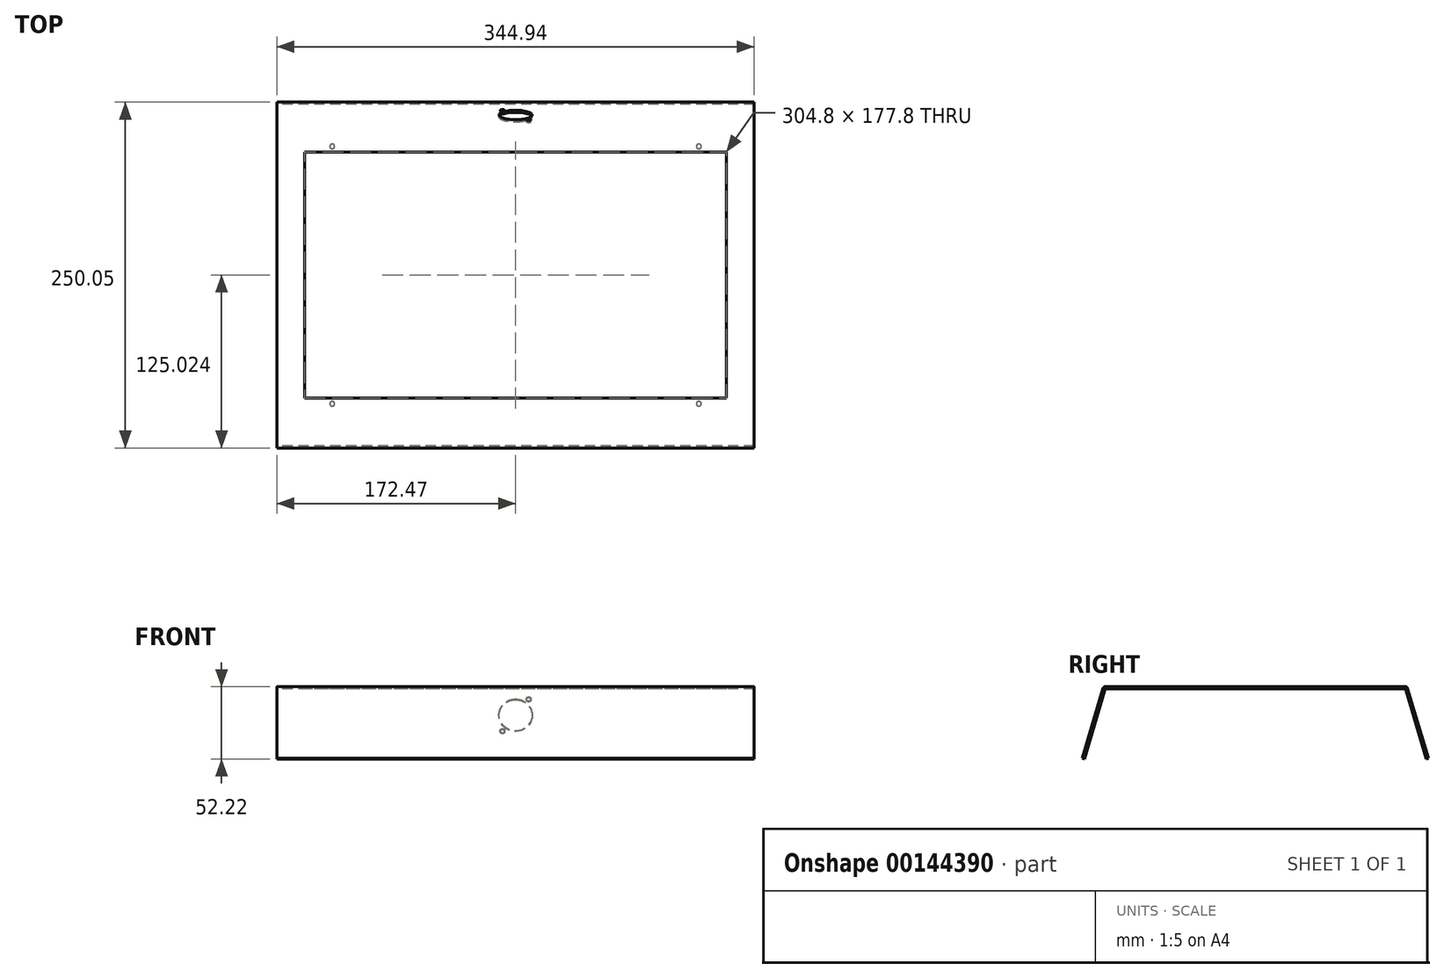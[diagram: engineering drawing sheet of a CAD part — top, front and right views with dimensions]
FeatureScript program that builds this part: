
annotation { "Feature Type Name" : "Feature", "Feature Type Description" : "" }
export const myFeature = defineFeature(function(context is Context, id is Id, definition is map)
    precondition{}
    {
        {
            var Q0;
            Q0=qCreatedBy(makeId("Right.planeOp"),FACE);
            var sketch = newSketch(context, id + "F0", { "sketchPlane" : qUnion([Q0])});
            skLineSegment(sketch, "E0", {"start": v(-135.27, 0) * mm, "end": v(-120.25, 50.63) * mm});
            skLineSegment(sketch, "E1", {"start": v(-118.72, 51.77) * mm, "end": v(98.23, 51.77) * mm});
            skLineSegment(sketch, "E2", {"start": v(99.75, 50.63) * mm, "end": v(114.78, 0) * mm});
            skLineSegment(sketch, "E3.0", {"start": v(98.57, 49.05) * mm, "end": v(113.25, -0.45) * mm});
            skLineSegment(sketch, "E3.1", {"start": v(-117.54, 50.18) * mm, "end": v(97.05, 50.18) * mm});
            skLineSegment(sketch, "E3.2", {"start": v(-133.75, -0.45) * mm, "end": v(-119.06, 49.05) * mm});
            skLineSegment(sketch, "E4", {"start": v(-135.27, 0) * mm, "end": v(-133.75, -0.45) * mm});
            skLineSegment(sketch, "E5", {"start": v(113.25, -0.45) * mm, "end": v(114.78, 0) * mm});
            skLineSegment(sketch, "E6", {"start": v(-133.75, -0.45) * mm, "end": v(113.25, -0.45) * mm, "construction": true});
            skLineSegment(sketch, "E7", {"start": v(129.46, -0.45) * mm, "end": v(129.46, 50.18) * mm, "construction": true});
            skPoint(sketch, "E8.visualSharp", {"position": v(-118.72, 50.18) * mm});
            skArc(sketch, "E8.filletArc", {"start": v(-117.54, 50.18) * mm, "mid": v(-118.49, 49.87) * mm, "end": v(-119.06, 49.05) * mm});
            skPoint(sketch, "E9.visualSharp", {"position": v(-119.9, 51.77) * mm});
            skArc(sketch, "E9.filletArc", {"start": v(-118.72, 51.77) * mm, "mid": v(-119.67, 51.45) * mm, "end": v(-120.25, 50.63) * mm});
            skPoint(sketch, "E10.visualSharp", {"position": v(98.23, 50.18) * mm});
            skArc(sketch, "E10.filletArc", {"start": v(98.57, 49.05) * mm, "mid": v(98, 49.87) * mm, "end": v(97.05, 50.18) * mm});
            skPoint(sketch, "E11.visualSharp", {"position": v(99.42, 51.77) * mm});
            skArc(sketch, "E11.filletArc", {"start": v(99.75, 50.63) * mm, "mid": v(99.18, 51.45) * mm, "end": v(98.23, 51.77) * mm});
            skSolve(sketch);
        }
        {
            var Q0;
            Q0=qSketchRegion(id+"F0",true);
            extrude(context, id + "F1", {"entities" : qUnion([Q0]), "endBound" : BoundingType.SYMMETRIC, "depth" : 344.93 * mm});
        }
        {
            var Q0;
            Q0=makeQuery(id+"F1.opExtrude","SWEPT_FACE",FACE,{"disambiguationData":[OSD([sQuery(id+"F0.wireOp",EDGE,"E1")])]});
            var sketch = newSketch(context, id + "F2", { "sketchPlane" : qUnion([Q0])});
            skLineSegment(sketch, "E12.bottom", {"start": v(-152.4, 78.65) * mm, "end": v(152.4, 78.65) * mm});
            skLineSegment(sketch, "E12.top", {"start": v(-152.4, -99.15) * mm, "end": v(152.4, -99.15) * mm});
            skLineSegment(sketch, "E12.left", {"start": v(-152.4, 78.65) * mm, "end": v(-152.4, -99.15) * mm});
            skLineSegment(sketch, "E12.right", {"start": v(152.4, 78.65) * mm, "end": v(152.4, -99.15) * mm});
            skPoint(sketch, "E12.middle", {"position": v(27.76, -10.25) * mm});
            skPoint(sketch, "E13", {"position": v(-172.47, -10.25) * mm});
            skPoint(sketch, "E14", {"position": v(0, 98.23) * mm});
            skPoint(sketch, "E15", {"position": v(-152.4, -10.25) * mm});
            skPoint(sketch, "E16", {"position": v(0, 78.65) * mm});
            skSolve(sketch);
        }
        {
            var Q0;
            Q0=qSketchRegion(id+"F2",true);
            extrude(context, id + "F3", {"entities" : qUnion([Q0]), "operationType" : NewBodyOperationType.REMOVE, "endBound" : BoundingType.SYMMETRIC, "depth" : 25.4 * mm});
        }
        {
            var Q0;
            Q0=makeQuery(id+"F1.opExtrude","SWEPT_FACE",FACE,{"disambiguationData":[OSD([sQuery(id+"F0.wireOp",EDGE,"E2")])]});
            var sketch = newSketch(context, id + "F4", { "sketchPlane" : qUnion([Q0])});
            skPoint(sketch, "E17", {"position": v(-358.6, -1.14) * mm});
            skPoint(sketch, "E18", {"position": v(-172.47, -6.24) * mm});
            skPoint(sketch, "E19", {"position": v(0, 20.17) * mm});
            skPoint(sketch, "E20", {"position": v(0, 0) * mm});
            skPoint(sketch, "E21", {"position": v(-9.5, 12) * mm});
            skPoint(sketch, "E22", {"position": v(9.5, -12) * mm});
            skSolve(sketch);
        }
        {
            var Q0;
            Q0=makeQuery(id+"F1.opExtrude","SWEPT_FACE",FACE,{"disambiguationData":[OSD([sQuery(id+"F0.wireOp",EDGE,"E3.1")])]});
            var sketch = newSketch(context, id + "F5", { "sketchPlane" : qUnion([Q0])});
            skCircle(sketch, "E23", {"center": v(132.47, -82.75) * mm, "radius": 1.75 * mm});
            skCircle(sketch, "E24", {"center": v(132.47, 103.25) * mm, "radius": 1.75 * mm});
            skCircle(sketch, "E25", {"center": v(-132.47, 103.25) * mm, "radius": 1.75 * mm});
            skCircle(sketch, "E26", {"center": v(-132.47, -82.75) * mm, "radius": 1.75 * mm});
            skSolve(sketch);
        }
        {
            var Q0;
            Q0=qSketchRegion(id+"F5",true);
            extrude(context, id + "F6", {"entities" : qUnion([Q0]), "operationType" : NewBodyOperationType.ADD, "depth" : 5 / 203.2 * mm});
        }
        {
            var Q0;
            Q0=sQuery(id+"F4.wireOp",VERTEX,"E21");
            var Q1;
            Q1=makeQuery(id+"F1.opExtrude","SWEPT_BODY",BODY,{"disambiguationData":[OSD([sQuery(id+"F0.wireOp",EDGE,"E0"),sQuery(id+"F0.wireOp",EDGE,"E1"),sQuery(id+"F0.wireOp",EDGE,"E2"),sQuery(id+"F0.wireOp",EDGE,"E3.0"),sQuery(id+"F0.wireOp",EDGE,"E3.1"),sQuery(id+"F0.wireOp",EDGE,"E3.2"),sQuery(id+"F0.wireOp",EDGE,"E4"),sQuery(id+"F0.wireOp",EDGE,"E5")])]});
            hole(context, id + "F7", {"style" : HoleStyle.SIMPLE, "endStyle" : HoleEndStyle.THROUGH, "standardTappedOrClearance" : lookupTablePath({ "standard" : "ISO", "fit" : "Normal", "size" : "M3", "type" : "Clearance" }), "standardBlindInLast" : lookupTablePath({ "fit" : "Standard", "standard" : "ISO", "size" : "M3", "type" : "Clearance" }), "holeDiameter" : 3.3 * mm, "locations" : qUnion([Q0]), "scope" : qUnion([Q1]), "isTappedThrough" : true});
        }
        {
            var Q0;
            Q0=sQuery(id+"F4.wireOp",VERTEX,"E22");
            var Q1;
            Q1=makeQuery(id+"F1.opExtrude","SWEPT_BODY",BODY,{"disambiguationData":[OSD([sQuery(id+"F0.wireOp",EDGE,"E0"),sQuery(id+"F0.wireOp",EDGE,"E1"),sQuery(id+"F0.wireOp",EDGE,"E2"),sQuery(id+"F0.wireOp",EDGE,"E3.0"),sQuery(id+"F0.wireOp",EDGE,"E3.1"),sQuery(id+"F0.wireOp",EDGE,"E3.2"),sQuery(id+"F0.wireOp",EDGE,"E4"),sQuery(id+"F0.wireOp",EDGE,"E5")])]});
            hole(context, id + "F8", {"style" : HoleStyle.SIMPLE, "endStyle" : HoleEndStyle.THROUGH, "standardTappedOrClearance" : lookupTablePath({ "standard" : "ISO", "fit" : "Normal", "size" : "M3", "type" : "Clearance" }), "standardBlindInLast" : lookupTablePath({ "fit" : "Standard", "standard" : "ISO", "size" : "M3", "type" : "Clearance" }), "holeDiameter" : 3.3 * mm, "locations" : qUnion([Q0]), "scope" : qUnion([Q1]), "isTappedThrough" : true});
        }
        {
            var Q0;
            Q0=sQuery(id+"F4.wireOp",VERTEX,"E20");
            var Q1;
            Q1=makeQuery(id+"F1.opExtrude","SWEPT_BODY",BODY,{"disambiguationData":[OSD([sQuery(id+"F0.wireOp",EDGE,"E0"),sQuery(id+"F0.wireOp",EDGE,"E1"),sQuery(id+"F0.wireOp",EDGE,"E2"),sQuery(id+"F0.wireOp",EDGE,"E3.0"),sQuery(id+"F0.wireOp",EDGE,"E3.1"),sQuery(id+"F0.wireOp",EDGE,"E3.2"),sQuery(id+"F0.wireOp",EDGE,"E4"),sQuery(id+"F0.wireOp",EDGE,"E5")])]});
            hole(context, id + "F9", {"style" : HoleStyle.SIMPLE, "endStyle" : HoleEndStyle.THROUGH, "holeDiameter" : 24 * mm, "locations" : qUnion([Q0]), "scope" : qUnion([Q1]), "isTappedThrough" : true});
        }
    });
